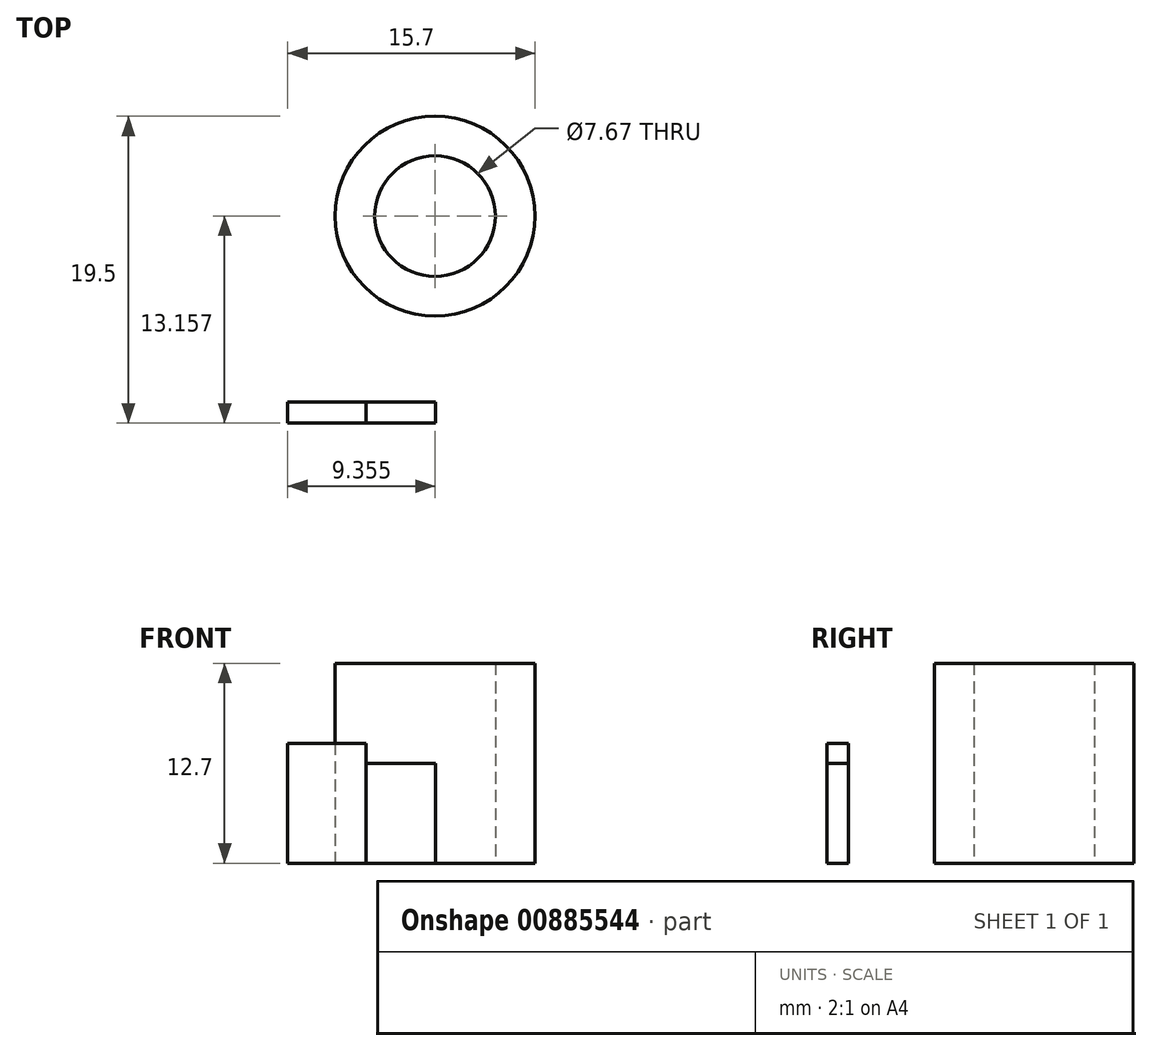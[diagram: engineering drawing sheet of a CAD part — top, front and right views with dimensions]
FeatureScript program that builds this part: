
annotation { "Feature Type Name" : "Feature", "Feature Type Description" : "" }
export const myFeature = defineFeature(function(context is Context, id is Id, definition is map)
    precondition{}
    {
        {
            var Q0;
            Q0=qCreatedBy(makeId("Top.planeOp"),FACE);
            var sketch = newSketch(context, id + "F0", { "sketchPlane" : qUnion([Q0])});
            skLineSegment(sketch, "E0.bottom", {"start": v(0, 0) * mm, "end": v(9.37, 0) * mm});
            skLineSegment(sketch, "E0.top", {"start": v(0, 11.78) * mm, "end": v(9.37, 11.78) * mm});
            skLineSegment(sketch, "E0.left", {"start": v(0, 0) * mm, "end": v(0, 11.78) * mm});
            skLineSegment(sketch, "E0.right", {"start": v(9.37, 0) * mm, "end": v(9.37, 11.78) * mm});
            skLineSegment(sketch, "E1.bottom", {"start": v(4.98, -1.36) * mm, "end": v(9.37, -1.36) * mm});
            skLineSegment(sketch, "E1.top", {"start": v(4.98, 0) * mm, "end": v(9.37, 0) * mm});
            skLineSegment(sketch, "E1.left", {"start": v(4.98, -1.36) * mm, "end": v(4.98, 0) * mm});
            skLineSegment(sketch, "E1.right", {"start": v(9.37, -1.36) * mm, "end": v(9.37, 0) * mm});
            skLineSegment(sketch, "E2.bottom", {"start": v(4.98, -1.36) * mm, "end": v(0, -1.36) * mm});
            skLineSegment(sketch, "E2.top", {"start": v(4.98, 0) * mm, "end": v(0, 0) * mm});
            skLineSegment(sketch, "E2.right", {"start": v(0, -1.36) * mm, "end": v(0, 0) * mm});
            skSolve(sketch);
        }
        {
            var Q0;
            Q0=makeQuery(id+"F0.imprint","IMPRINT",FACE,{"disambiguationData":[TD([[makeQuery(id+"F0.imprint","IMPRINT",EDGE,{"derivedFrom":sQuery(id+"F0.wireOp",EDGE,"E1.bottom")}),1.0]])]});
            extrude(context, id + "F1", {"entities" : qUnion([Q0]), "depth" : 6.35 * mm, "offsetDistance" : 25.4 * mm});
        }
        {
            var Q0;
            Q0=makeQuery(id+"F0.imprint","IMPRINT",FACE,{"disambiguationData":[TD([[makeQuery(id+"F0.imprint","IMPRINT",EDGE,{"derivedFrom":sQuery(id+"F0.wireOp",EDGE,"E2.bottom")}),-1.0]])]});
            extrude(context, id + "F2", {"entities" : qUnion([Q0]), "depth" : 7.62 * mm, "offsetDistance" : 25.4 * mm});
        }
        {
            var Q0;
            Q0=qCreatedBy(makeId("Top.planeOp"),FACE);
            var sketch = newSketch(context, id + "F3", { "sketchPlane" : qUnion([Q0])});
            skCircle(sketch, "E3", {"center": v(9.35, 11.8) * mm, "radius": 6.35 * mm});
            skCircle(sketch, "E4", {"center": v(9.35, 11.8) * mm, "radius": 3.83 * mm});
            skSolve(sketch);
        }
        {
            var Q0;
            Q0=makeQuery(id+"F3.imprint","IMPRINT",FACE,{"disambiguationData":[TD([[makeQuery(id+"F3.imprint","IMPRINT",EDGE,{"derivedFrom":sQuery(id+"F3.wireOp",EDGE,"E3")}),1.0]])]});
            extrude(context, id + "F4", {"entities" : qUnion([Q0]), "depth" : 12.7 * mm, "offsetDistance" : 25.4 * mm});
        }
    });
